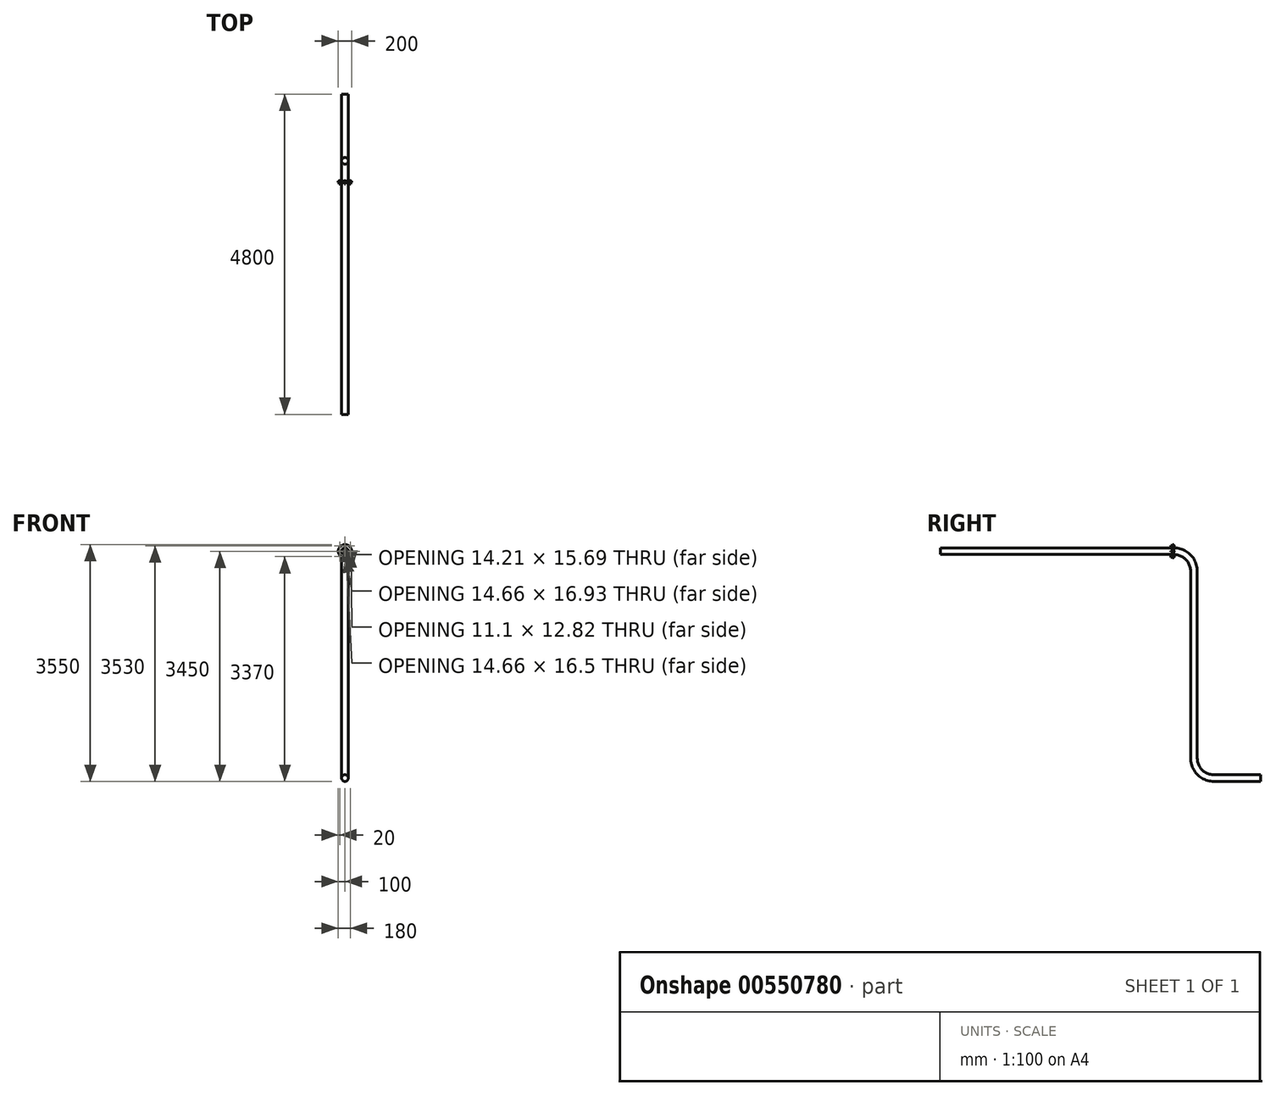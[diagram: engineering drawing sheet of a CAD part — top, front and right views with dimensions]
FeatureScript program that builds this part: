
annotation { "Feature Type Name" : "Feature", "Feature Type Description" : "" }
export const myFeature = defineFeature(function(context is Context, id is Id, definition is map)
    precondition{}
    {
        {
            var Q0;
            Q0=qCreatedBy(makeId("Front.planeOp"),FACE);
            var sketch = newSketch(context, id + "F0", { "sketchPlane" : qUnion([Q0])});
            skCircle(sketch, "E0", {"center": v(0, 0) * mm, "radius": 50 * mm});
            skSolve(sketch);
        }
        {
            var Q0;
            Q0=qCreatedBy(makeId("Right.planeOp"),FACE);
            var sketch = newSketch(context, id + "F1", { "sketchPlane" : qUnion([Q0])});
            skLineSegment(sketch, "E1", {"start": v(0, 0) * mm, "end": v(3500, 0) * mm});
            skLineSegment(sketch, "E2", {"start": v(3800, -300) * mm, "end": v(3800, -3100) * mm});
            skLineSegment(sketch, "E3", {"start": v(4100, -3400) * mm, "end": v(4800, -3400) * mm});
            skPoint(sketch, "E4.visualSharp", {"position": v(3800, 0) * mm});
            skArc(sketch, "E4.filletArc", {"start": v(3800, -300) * mm, "mid": v(3712.13, -87.87) * mm, "end": v(3500, 0) * mm});
            skPoint(sketch, "E5.visualSharp", {"position": v(3800, -3400) * mm});
            skArc(sketch, "E5.filletArc", {"start": v(3800, -3100) * mm, "mid": v(3887.87, -3312.13) * mm, "end": v(4100, -3400) * mm});
            skSolve(sketch);
        }
        {
            var Q0;
            Q0=makeQuery(id+"F0.imprint","IMPRINT",FACE,{"disambiguationData":[TD([[makeQuery(id+"F0.imprint","IMPRINT",EDGE,{"derivedFrom":sQuery(id+"F0.wireOp",EDGE,"E0")}),1.0]])]});
            var Q1;
            Q1=sQuery(id+"F1.wireOp",EDGE,"E1");
            var Q2;
            Q2=sQuery(id+"F1.wireOp",EDGE,"E4.filletArc");
            var Q3;
            Q3=sQuery(id+"F1.wireOp",EDGE,"E2");
            var Q4;
            Q4=sQuery(id+"F1.wireOp",EDGE,"E5.filletArc");
            var Q5;
            Q5=sQuery(id+"F1.wireOp",EDGE,"E3");
            sweep(context, id + "F2", {"profiles" : qUnion([Q0]), "path" : qUnion([Q1, Q2, Q3, Q4, Q5])});
        }
        {
            var Q0;
            Q0=qCreatedBy(makeId("Front.planeOp"),FACE);
            cPlane(context, id + "F3", {"entities" : qUnion([Q0]), "cplaneType" : CPlaneType.OFFSET, "offset" : 3500 * mm, "oppositeDirection" : true, "width" : 150 * mm, "height" : 150 * mm});
        }
        {
            var Q0;
            Q0=qCreatedBy(id+"F3.planeOp",FACE);
            var sketch = newSketch(context, id + "F4", { "sketchPlane" : qUnion([Q0])});
            skCircle(sketch, "E6", {"center": v(0, 0) * mm, "radius": 100 * mm});
            skSolve(sketch);
        }
        {
            var Q0;
            Q0=makeQuery(id+"F4.imprint","IMPRINT",FACE,{"disambiguationData":[TD([[makeQuery(id+"F4.imprint","IMPRINT",EDGE,{"derivedFrom":sQuery(id+"F4.wireOp",EDGE,"E6")}),1.0]])]});
            var Q1;
            Q1=sQuery(id+"F4.wireOp",EDGE,"E6");
            extrude(context, id + "F5", {"entities" : qUnion([Q0]), "operationType" : NewBodyOperationType.ADD, "surfaceEntities" : qUnion([Q1]), "depth" : 20 * mm, "offsetDistance" : 25 * mm});
        }
        {
            var Q0;
            Q0=makeQuery(id+"F5.opExtrude","CAP_FACE",FACE,{"disambiguationData":[OSD([sQuery(id+"F4.wireOp",EDGE,"E6")])],"isStart":false});
            var sketch = newSketch(context, id + "F6", { "sketchPlane" : qUnion([Q0])});
            skCircle(sketch, "E7.cCircle", {"center": v(0, 80) * mm, "radius": 7.15 * mm, "construction": true});
            skLineSegment(sketch, "E7.0", {"start": v(7.33, 83.8) * mm, "end": v(6.96, 75.55) * mm});
            skLineSegment(sketch, "E7.1", {"start": v(6.96, 75.55) * mm, "end": v(-0.37, 71.75) * mm});
            skLineSegment(sketch, "E7.2", {"start": v(-0.37, 71.75) * mm, "end": v(-7.33, 76.2) * mm});
            skLineSegment(sketch, "E7.3", {"start": v(-7.33, 76.2) * mm, "end": v(-6.96, 84.45) * mm});
            skLineSegment(sketch, "E7.4", {"start": v(-6.96, 84.45) * mm, "end": v(0.37, 88.25) * mm});
            skLineSegment(sketch, "E7.5", {"start": v(0.37, 88.25) * mm, "end": v(7.33, 83.8) * mm});
            skPoint(sketch, "E7.0.midPoint", {"position": v(7.15, 79.68) * mm});
            skCircle(sketch, "E8.cCircle", {"center": v(80, 0) * mm, "radius": 5.55 * mm, "construction": true});
            skLineSegment(sketch, "E8.0", {"start": v(85.55, 3.2) * mm, "end": v(85.55, -3.2) * mm});
            skLineSegment(sketch, "E8.1", {"start": v(85.55, -3.2) * mm, "end": v(80, -6.41) * mm});
            skLineSegment(sketch, "E8.2", {"start": v(80, -6.41) * mm, "end": v(74.45, -3.2) * mm});
            skLineSegment(sketch, "E8.3", {"start": v(74.45, -3.2) * mm, "end": v(74.45, 3.2) * mm});
            skLineSegment(sketch, "E8.4", {"start": v(74.45, 3.2) * mm, "end": v(80, 6.41) * mm});
            skLineSegment(sketch, "E8.5", {"start": v(80, 6.41) * mm, "end": v(85.55, 3.2) * mm});
            skPoint(sketch, "E8.0.midPoint", {"position": v(85.55, 0) * mm});
            skCircle(sketch, "E9.cCircle", {"center": v(0, -80) * mm, "radius": 7.33 * mm, "construction": true});
            skLineSegment(sketch, "E9.0", {"start": v(7.33, -75.77) * mm, "end": v(7.33, -84.23) * mm});
            skLineSegment(sketch, "E9.1", {"start": v(7.33, -84.23) * mm, "end": v(0, -88.46) * mm});
            skLineSegment(sketch, "E9.2", {"start": v(0, -88.46) * mm, "end": v(-7.33, -84.23) * mm});
            skLineSegment(sketch, "E9.3", {"start": v(-7.33, -84.23) * mm, "end": v(-7.33, -75.77) * mm});
            skLineSegment(sketch, "E9.4", {"start": v(-7.33, -75.77) * mm, "end": v(0, -71.54) * mm});
            skLineSegment(sketch, "E9.5", {"start": v(0, -71.54) * mm, "end": v(7.33, -75.77) * mm});
            skPoint(sketch, "E9.0.midPoint", {"position": v(7.33, -80) * mm});
            skCircle(sketch, "E10.cCircle", {"center": v(-80, 0) * mm, "radius": 6.82 * mm, "construction": true});
            skLineSegment(sketch, "E10.0", {"start": v(-72.9, -3.38) * mm, "end": v(-79.38, -7.85) * mm});
            skLineSegment(sketch, "E10.1", {"start": v(-79.38, -7.85) * mm, "end": v(-86.48, -4.46) * mm});
            skLineSegment(sketch, "E10.2", {"start": v(-86.48, -4.46) * mm, "end": v(-87.1, 3.38) * mm});
            skLineSegment(sketch, "E10.3", {"start": v(-87.1, 3.38) * mm, "end": v(-80.62, 7.85) * mm});
            skLineSegment(sketch, "E10.4", {"start": v(-80.62, 7.85) * mm, "end": v(-73.52, 4.46) * mm});
            skLineSegment(sketch, "E10.5", {"start": v(-73.52, 4.46) * mm, "end": v(-72.9, -3.38) * mm});
            skPoint(sketch, "E10.0.midPoint", {"position": v(-76.14, -5.62) * mm});
            skSolve(sketch);
        }
        {
            var Q0;
            Q0 = qSketchRegion(id + "F6", true);
            extrude(context, id + "F7", {"entities" : qUnion([Q0]), "operationType" : NewBodyOperationType.ADD, "endBound" : BoundingType.SYMMETRIC, "depth" : 50 * mm, "offsetDistance" : 25 * mm});
        }
    });
